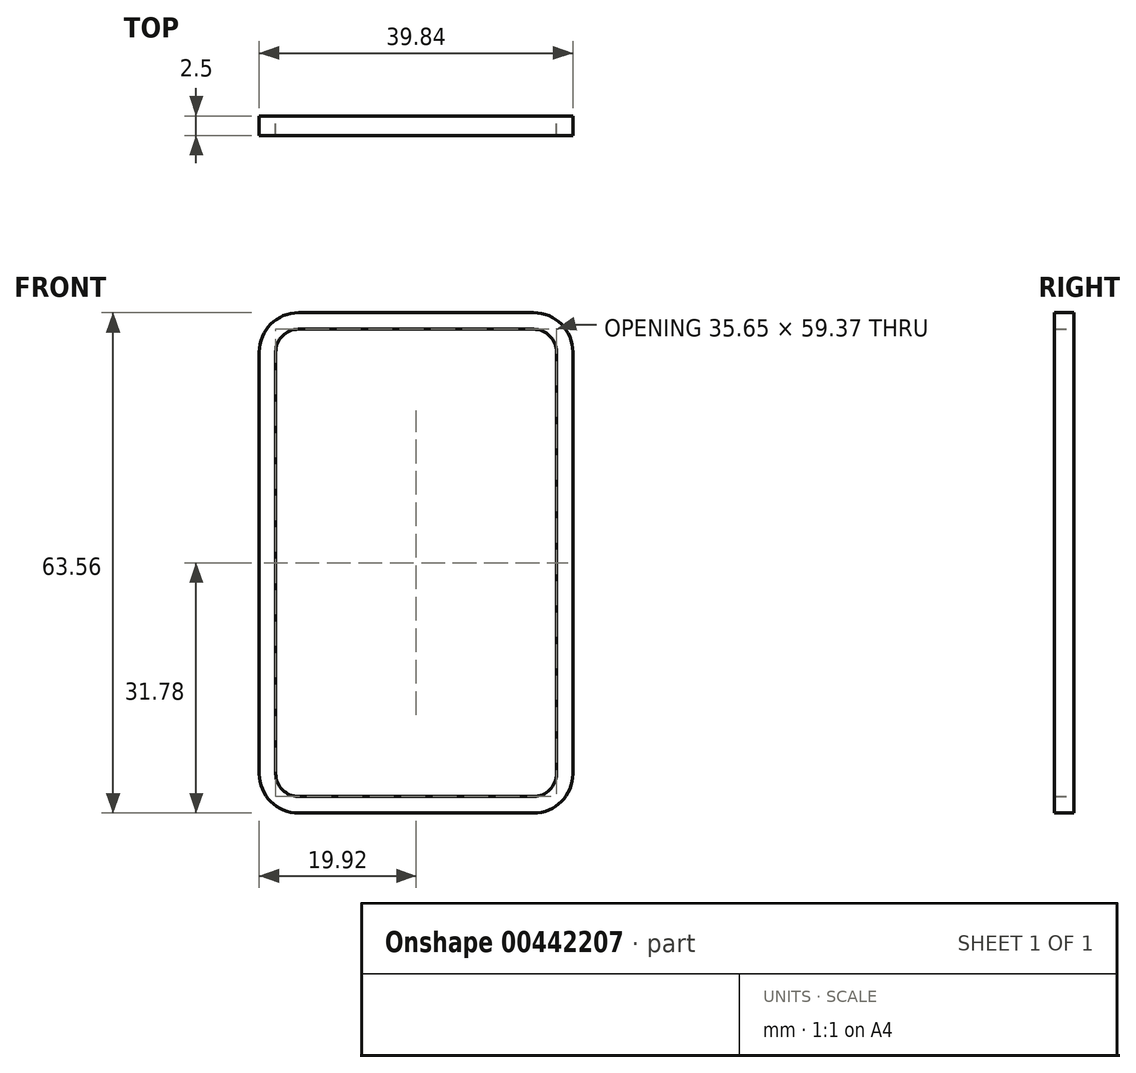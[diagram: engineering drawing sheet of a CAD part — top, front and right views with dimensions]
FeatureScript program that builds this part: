
annotation { "Feature Type Name" : "Feature", "Feature Type Description" : "" }
export const myFeature = defineFeature(function(context is Context, id is Id, definition is map)
    precondition{}
    {
        {
            var Q0;
            Q0=qCreatedBy(makeId("Front.planeOp"),FACE);
            var sketch = newSketch(context, id + "F0", { "sketchPlane" : qUnion([Q0])});
            skLineSegment(sketch, "E0.bottom", {"start": v(14.92, 31.78) * mm, "end": v(-14.92, 31.78) * mm});
            skLineSegment(sketch, "E0.top", {"start": v(14.92, -31.78) * mm, "end": v(-14.92, -31.78) * mm});
            skLineSegment(sketch, "E0.left", {"start": v(19.92, 26.78) * mm, "end": v(19.92, -26.78) * mm});
            skLineSegment(sketch, "E0.right", {"start": v(-19.92, 26.78) * mm, "end": v(-19.92, -26.78) * mm});
            skPoint(sketch, "E0.middle", {"position": v(0, 0) * mm});
            skPoint(sketch, "E1.visualSharp", {"position": v(19.92, 31.78) * mm});
            skArc(sketch, "E1.filletArc", {"start": v(19.92, 26.78) * mm, "mid": v(18.46, 30.32) * mm, "end": v(14.92, 31.78) * mm});
            skPoint(sketch, "E2.visualSharp", {"position": v(-19.92, 31.78) * mm});
            skArc(sketch, "E2.filletArc", {"start": v(-14.92, 31.78) * mm, "mid": v(-18.46, 30.32) * mm, "end": v(-19.92, 26.78) * mm});
            skPoint(sketch, "E3.visualSharp", {"position": v(-19.92, -31.78) * mm});
            skArc(sketch, "E3.filletArc", {"start": v(-19.92, -26.78) * mm, "mid": v(-18.46, -30.32) * mm, "end": v(-14.92, -31.78) * mm});
            skPoint(sketch, "E4.visualSharp", {"position": v(19.92, -31.78) * mm});
            skArc(sketch, "E4.filletArc", {"start": v(14.92, -31.78) * mm, "mid": v(18.46, -30.32) * mm, "end": v(19.92, -26.78) * mm});
            skArc(sketch, "E5.0", {"start": v(17.82, 26.78) * mm, "mid": v(16.98, 28.84) * mm, "end": v(14.92, 29.68) * mm});
            skLineSegment(sketch, "E5.1", {"start": v(17.82, 26.78) * mm, "end": v(17.82, -26.78) * mm});
            skLineSegment(sketch, "E5.2", {"start": v(14.92, 29.68) * mm, "end": v(-14.92, 29.68) * mm});
            skArc(sketch, "E5.3", {"start": v(14.92, -29.68) * mm, "mid": v(16.98, -28.84) * mm, "end": v(17.82, -26.78) * mm});
            skArc(sketch, "E5.4", {"start": v(-14.92, 29.68) * mm, "mid": v(-16.98, 28.84) * mm, "end": v(-17.82, 26.78) * mm});
            skLineSegment(sketch, "E5.5", {"start": v(-17.82, 26.78) * mm, "end": v(-17.82, -26.78) * mm});
            skArc(sketch, "E5.6", {"start": v(-17.82, -26.78) * mm, "mid": v(-16.98, -28.84) * mm, "end": v(-14.92, -29.68) * mm});
            skLineSegment(sketch, "E5.7", {"start": v(14.92, -29.68) * mm, "end": v(-14.92, -29.68) * mm});
            skSolve(sketch);
        }
        {
            var Q0;
            Q0=makeQuery(id+"F0.imprint","IMPRINT",FACE,{"disambiguationData":[TD([[makeQuery(id+"F0.imprint","IMPRINT",EDGE,{"derivedFrom":sQuery(id+"F0.wireOp",EDGE,"E0.bottom")}),1.0]])]});
            extrude(context, id + "F1", {"entities" : qUnion([Q0]), "depth" : 2.5 * mm});
        }
    });
